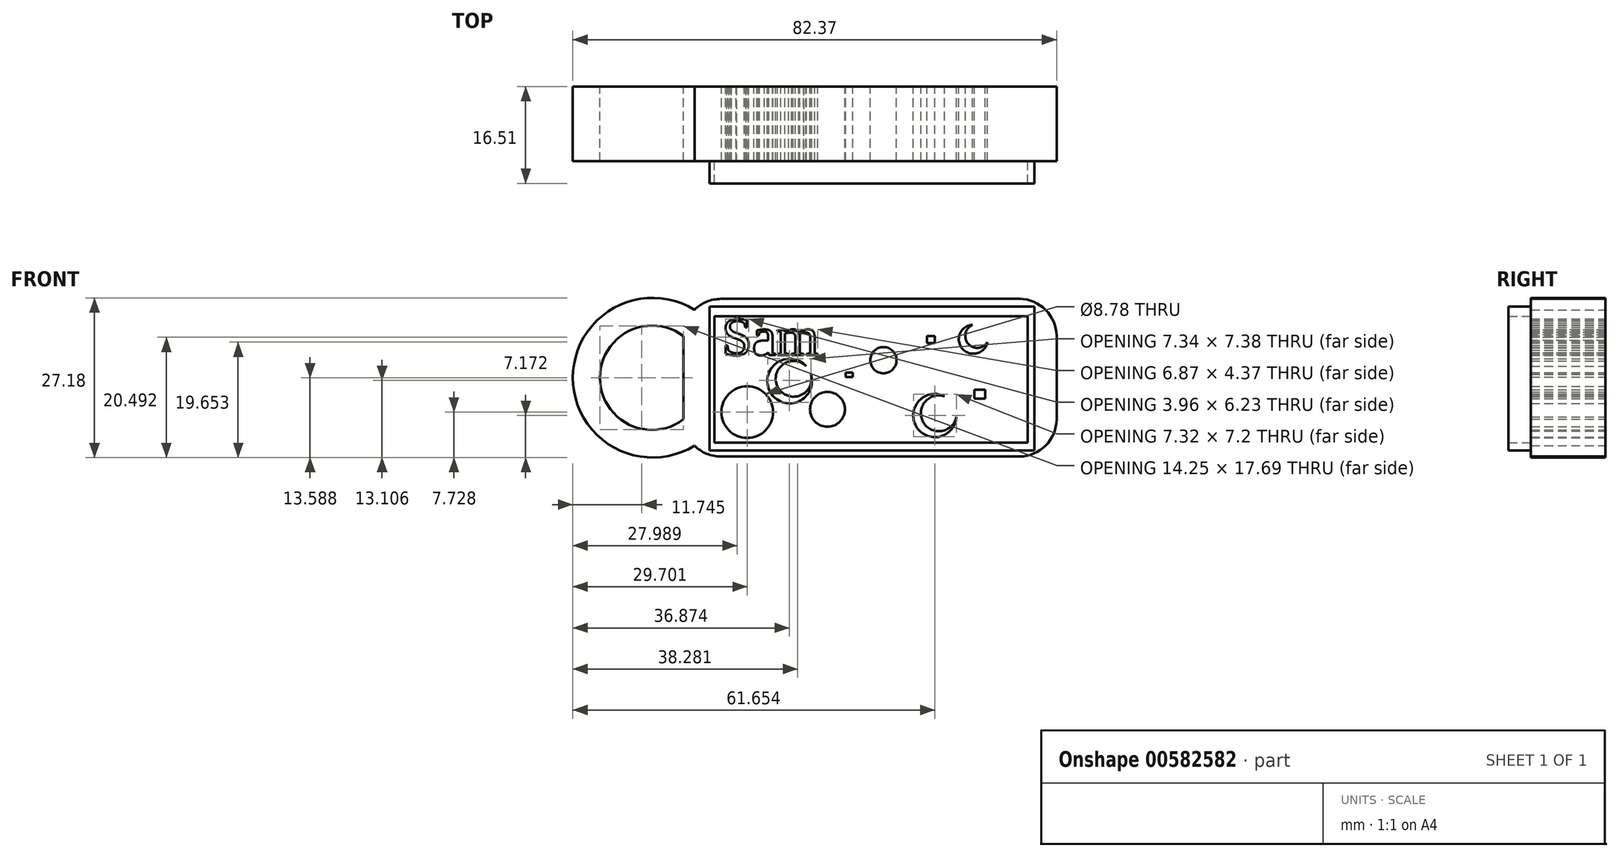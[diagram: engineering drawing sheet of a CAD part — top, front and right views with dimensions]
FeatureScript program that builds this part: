
annotation { "Feature Type Name" : "Feature", "Feature Type Description" : "" }
export const myFeature = defineFeature(function(context is Context, id is Id, definition is map)
    precondition{}
    {
        {
            var Q0;
            Q0=qCreatedBy(makeId("Front.planeOp"),FACE);
            var sketch = newSketch(context, id + "F0", { "sketchPlane" : qUnion([Q0])});
            skLineSegment(sketch, "E0.bottom", {"start": v(-33.43, 12.56) * mm, "end": v(17.37, 12.56) * mm});
            skLineSegment(sketch, "E0.top", {"start": v(-33.43, -14.29) * mm, "end": v(17.37, -14.29) * mm});
            skLineSegment(sketch, "E0.left", {"start": v(-39.78, 6.21) * mm, "end": v(-39.78, -7.94) * mm});
            skLineSegment(sketch, "E0.right", {"start": v(23.72, 6.21) * mm, "end": v(23.72, -7.94) * mm});
            skPoint(sketch, "E1.visualSharp", {"position": v(-39.78, 12.56) * mm});
            skArc(sketch, "E1.filletArc", {"start": v(-33.43, 12.56) * mm, "mid": v(-37.92, 10.7) * mm, "end": v(-39.78, 6.21) * mm});
            skPoint(sketch, "E2.visualSharp", {"position": v(23.72, 12.56) * mm});
            skArc(sketch, "E2.filletArc", {"start": v(23.72, 6.21) * mm, "mid": v(21.86, 10.7) * mm, "end": v(17.37, 12.56) * mm});
            skPoint(sketch, "E3.visualSharp", {"position": v(23.72, -14.29) * mm});
            skArc(sketch, "E3.filletArc", {"start": v(17.37, -14.29) * mm, "mid": v(21.86, -12.43) * mm, "end": v(23.72, -7.94) * mm});
            skPoint(sketch, "E4.visualSharp", {"position": v(-39.78, -14.29) * mm});
            skArc(sketch, "E4.filletArc", {"start": v(-39.78, -7.94) * mm, "mid": v(-37.92, -12.43) * mm, "end": v(-33.43, -14.29) * mm});
            skText(sketch, "E5", { "text": "Sam", "fontName": "Tinos-Regular.ttf"});
            skLineSegment(sketch, "E6.left", {"start": v(-39.78, 3.67) * mm, "end": v(-39.78, -6.49) * mm});
            skPoint(sketch, "E7.visualSharp", {"position": v(-60.9, 6.21) * mm});
            skPoint(sketch, "E8.visualSharp", {"position": v(-60.9, -7.94) * mm});
            skPoint(sketch, "E9.visualSharp", {"position": v(-56.82, -6.49) * mm});
            skPoint(sketch, "E10.visualSharp", {"position": v(-56.82, 3.67) * mm});
            skArc(sketch, "E11", {"start": v(-37.92, 10.7) * mm, "mid": v(-58.65, -0.86) * mm, "end": v(-37.92, -12.43) * mm});
            skArc(sketch, "E12", {"start": v(-39.78, 6.21) * mm, "mid": v(-54.03, -0.86) * mm, "end": v(-39.78, -7.94) * mm});
            skLineSegment(sketch, "E13.left", {"start": v(-33.26, -5.88) * mm, "end": v(-33.26, -7.57) * mm});
            skCircle(sketch, "E14", {"center": v(-28.95, -6.72) * mm, "radius": 4.4 * mm});
            skCircle(sketch, "E15", {"center": v(-21.73, -1.43) * mm, "radius": 3.8 * mm});
            skCircle(sketch, "E16", {"center": v(-15.29, -6.24) * mm, "radius": 2.97 * mm});
            skCircle(sketch, "E17", {"center": v(-5.76, 2.13) * mm, "radius": 2.24 * mm});
            skCircle(sketch, "E18", {"center": v(3, -7.3) * mm, "radius": 3.68 * mm});
            skCircle(sketch, "E19", {"center": v(9.54, 5.69) * mm, "radius": 2.46 * mm});
            skLineSegment(sketch, "E20.bottom", {"start": v(1.65, 6.27) * mm, "end": v(3, 6.27) * mm});
            skLineSegment(sketch, "E20.top", {"start": v(1.65, 5.02) * mm, "end": v(3, 5.02) * mm});
            skLineSegment(sketch, "E20.left", {"start": v(1.65, 6.27) * mm, "end": v(1.65, 5.02) * mm});
            skLineSegment(sketch, "E20.right", {"start": v(3, 6.27) * mm, "end": v(3, 5.02) * mm});
            skLineSegment(sketch, "E21.bottom", {"start": v(9.73, -2.87) * mm, "end": v(11.56, -2.87) * mm});
            skLineSegment(sketch, "E21.top", {"start": v(9.73, -4.41) * mm, "end": v(11.56, -4.41) * mm});
            skLineSegment(sketch, "E21.left", {"start": v(9.73, -2.87) * mm, "end": v(9.73, -4.41) * mm});
            skLineSegment(sketch, "E21.right", {"start": v(11.56, -2.87) * mm, "end": v(11.56, -4.41) * mm});
            skLineSegment(sketch, "E22.bottom", {"start": v(-12.2, 0) * mm, "end": v(-10.96, 0) * mm});
            skLineSegment(sketch, "E22.top", {"start": v(-12.2, -0.76) * mm, "end": v(-10.96, -0.76) * mm});
            skLineSegment(sketch, "E22.left", {"start": v(-12.2, 0) * mm, "end": v(-12.2, -0.76) * mm});
            skLineSegment(sketch, "E22.right", {"start": v(-10.96, 0) * mm, "end": v(-10.96, -0.76) * mm});
            const initialGuessF0  = {"E5": [-0.03326, 0.00302, 1, 0, 0.00667]};
            skSetInitialGuess(sketch, initialGuessF0);
            skSolve(sketch);
        }
        {
            var Q0;
            Q0 = qSketchRegion(id + "F0", true);
            extrude(context, id + "F1", {"entities" : qUnion([Q0]), "depth" : 12.7 * mm, "offsetDistance" : 25.4 * mm});
        }
        {
            var Q0;
            Q0=qCreatedBy(makeId("Front.planeOp"),FACE);
            var sketch = newSketch(context, id + "F2", { "sketchPlane" : qUnion([Q0])});
            skLineSegment(sketch, "E23.bottom", {"start": v(-34.53, 9.63) * mm, "end": v(18.77, 9.63) * mm});
            skLineSegment(sketch, "E23.top", {"start": v(-34.53, -11.92) * mm, "end": v(18.77, -11.92) * mm});
            skLineSegment(sketch, "E23.left", {"start": v(-34.53, 9.63) * mm, "end": v(-34.53, -11.92) * mm});
            skLineSegment(sketch, "E23.right", {"start": v(18.77, 9.63) * mm, "end": v(18.77, -11.92) * mm});
            skLineSegment(sketch, "E24.bottom", {"start": v(-35.4, 11.27) * mm, "end": v(19.93, 11.27) * mm});
            skLineSegment(sketch, "E24.top", {"start": v(-35.4, -13.26) * mm, "end": v(19.93, -13.26) * mm});
            skLineSegment(sketch, "E24.left", {"start": v(-35.4, 11.27) * mm, "end": v(-35.4, -13.26) * mm});
            skLineSegment(sketch, "E24.right", {"start": v(19.93, 11.27) * mm, "end": v(19.93, -13.26) * mm});
            skSolve(sketch);
        }
        {
            var Q0;
            Q0 = qSketchRegion(id + "F2", true);
            extrude(context, id + "F3", {"entities" : qUnion([Q0]), "operationType" : NewBodyOperationType.ADD, "depth" : 16.5 * mm, "offsetDistance" : 25.4 * mm});
        }
        {
            var Q0;
            Q0=qCreatedBy(makeId("Front.planeOp"),FACE);
            var sketch = newSketch(context, id + "F4", { "sketchPlane" : qUnion([Q0])});
            skCircle(sketch, "E25", {"center": v(-21.06, -1.05) * mm, "radius": 3.04 * mm});
            skCircle(sketch, "E26", {"center": v(3.67, -6.91) * mm, "radius": 3.06 * mm});
            skCircle(sketch, "E27", {"center": v(10.21, 6.27) * mm, "radius": 2.04 * mm});
            skSolve(sketch);
        }
        {
            var Q0;
            Q0 = qSketchRegion(id + "F4", true);
            extrude(context, id + "F5", {"entities" : qUnion([Q0]), "operationType" : NewBodyOperationType.ADD, "depth" : 12.7 * mm, "offsetDistance" : 25.4 * mm});
        }
    });
